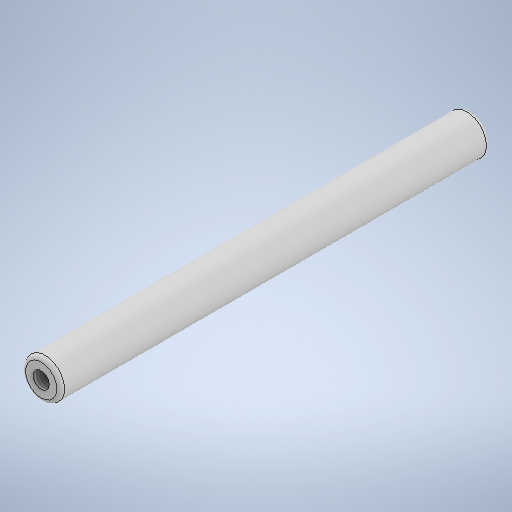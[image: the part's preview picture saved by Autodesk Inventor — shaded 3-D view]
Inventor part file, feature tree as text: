
AUTODESK INVENTOR PART (.ipt)
format: ipt  version: 2025.1 (Build 291241000, 241)  size: 272,384 bytes
history: native  units: mm
features: sketch x3, hole x2, revolve x1, fillet x1
ambient origin geometry x8: Origin, YZ Plane, XZ Plane, XY Plane, X Axis, Y Axis, Z Axis, Center Point
bodies: Solid1 (feature_tree)
feature tree (7):
  revolve  "Revolution1"  [1 undecoded]
  fillet  "Fillet1"  [1 undecoded]
  hole  "Hole1"  [1 undecoded]
  hole  "Hole2"  [1 undecoded]
  sketch  "Sketch1"  dims[d0=110.0mm d1=10.0mm d2=90.0deg]
  sketch  "Sketch2"  dims[d3=1.0mm]
  sketch  "Sketch3"  dims[d4=4.134mm d5=12.0mm d6=4.0mm d7=2.0mm d8=90.0deg d9=12.0mm d10=0.0mm d11=4.134mm d12=12.0mm d13=4.0mm d14=2.0mm d15=90.0deg d16=12.0mm d17=0.0mm]
note: 4 required parameter values undecoded (feature->parameter linkage not recoverable at this tier; creation-order binding heuristic only, values carry confidence <= 0.55)